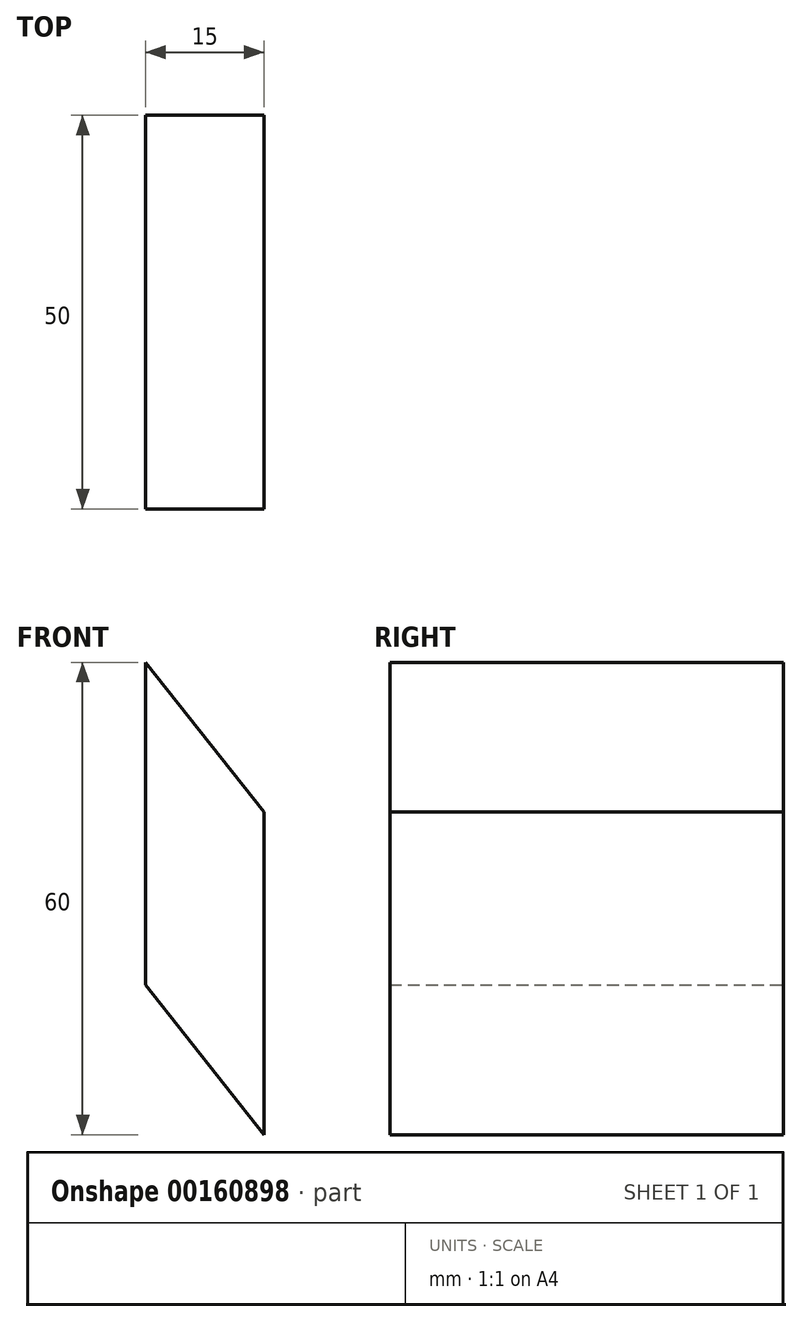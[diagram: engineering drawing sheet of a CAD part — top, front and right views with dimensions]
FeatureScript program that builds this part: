
annotation { "Feature Type Name" : "Feature", "Feature Type Description" : "" }
export const myFeature = defineFeature(function(context is Context, id is Id, definition is map)
    precondition{}
    {
        {
            var Q0;
            Q0=qCreatedBy(makeId("Front.planeOp"),FACE);
            var sketch = newSketch(context, id + "F0", { "sketchPlane" : qUnion([Q0])});
            skLineSegment(sketch, "E0.bottom", {"start": v(4.25, 26.75) * mm, "end": v(-4.25, 26.75) * mm, "construction": true});
            skLineSegment(sketch, "E0.top", {"start": v(4.25, -26.75) * mm, "end": v(-4.25, -26.75) * mm, "construction": true});
            skLineSegment(sketch, "E0.left", {"start": v(4.25, 26.75) * mm, "end": v(4.25, -26.75) * mm, "construction": true});
            skLineSegment(sketch, "E0.right", {"start": v(-4.25, 26.75) * mm, "end": v(-4.25, -26.75) * mm, "construction": true});
            skPoint(sketch, "E0.middle", {"position": v(0, 0) * mm});
            skArc(sketch, "E1", {"start": v(-1, 26.75) * mm, "mid": v(-4.25, 30) * mm, "end": v(-7.5, 26.75) * mm});
            skArc(sketch, "E2", {"start": v(1, -26.75) * mm, "mid": v(4.25, -30) * mm, "end": v(7.5, -26.75) * mm});
            skLineSegment(sketch, "E3", {"start": v(-7.5, 26.75) * mm, "end": v(-7.5, -7.75) * mm});
            skLineSegment(sketch, "E4", {"start": v(-4.25, -11) * mm, "end": v(-2.25, -11) * mm});
            skLineSegment(sketch, "E5", {"start": v(1, -14.25) * mm, "end": v(1, -26.75) * mm});
            skLineSegment(sketch, "E6", {"start": v(-1, 26.75) * mm, "end": v(-1, 14.25) * mm});
            skLineSegment(sketch, "E7", {"start": v(2.25, 11) * mm, "end": v(4.25, 11) * mm});
            skLineSegment(sketch, "E8", {"start": v(7.5, 7.75) * mm, "end": v(7.5, -26.75) * mm});
            skPoint(sketch, "E9.visualSharp", {"position": v(-1, 11) * mm});
            skArc(sketch, "E9.filletArc", {"start": v(-1, 14.25) * mm, "mid": v(-0.05, 11.95) * mm, "end": v(2.25, 11) * mm});
            skPoint(sketch, "E10.visualSharp", {"position": v(7.5, 11) * mm});
            skArc(sketch, "E10.filletArc", {"start": v(7.5, 7.75) * mm, "mid": v(6.55, 10.05) * mm, "end": v(4.25, 11) * mm});
            skPoint(sketch, "E11.visualSharp", {"position": v(-7.5, -11) * mm});
            skArc(sketch, "E11.filletArc", {"start": v(-7.5, -7.75) * mm, "mid": v(-6.55, -10.05) * mm, "end": v(-4.25, -11) * mm});
            skPoint(sketch, "E12.visualSharp", {"position": v(1, -11) * mm});
            skArc(sketch, "E12.filletArc", {"start": v(1, -14.25) * mm, "mid": v(0.05, -11.95) * mm, "end": v(-2.25, -11) * mm});
            skLineSegment(sketch, "E13", {"start": v(2.25, 11) * mm, "end": v(-2.25, -11) * mm, "construction": true});
            skLineSegment(sketch, "E14", {"start": v(-4.25, 30) * mm, "end": v(12.81, 30) * mm, "construction": true});
            skSolve(sketch);
        }
        {
            var Q0;
            Q0=qCreatedBy(makeId("Front.planeOp"),FACE);
            var sketch = newSketch(context, id + "F1", { "sketchPlane" : qUnion([Q0])});
            skLineSegment(sketch, "E15", {"start": v(-7.5, 30) * mm, "end": v(7.5, 11) * mm});
            skLineSegment(sketch, "E16", {"start": v(7.5, 11) * mm, "end": v(7.5, -30) * mm});
            skLineSegment(sketch, "E17", {"start": v(7.5, -30) * mm, "end": v(-7.5, -11) * mm});
            skLineSegment(sketch, "E18", {"start": v(-7.5, -11) * mm, "end": v(-7.5, 30) * mm});
            skSolve(sketch);
        }
        {
            var Q0;
            Q0=makeQuery(id+"F1.imprint","IMPRINT",FACE,{"disambiguationData":[TD([[makeQuery(id+"F1.imprint","IMPRINT",EDGE,{"derivedFrom":sQuery(id+"F1.wireOp",EDGE,"E15")}),-1.0]])]});
            extrude(context, id + "F2", {"entities" : qUnion([Q0]), "endBound" : BoundingType.SYMMETRIC, "depth" : 50 * mm});
        }
    });
